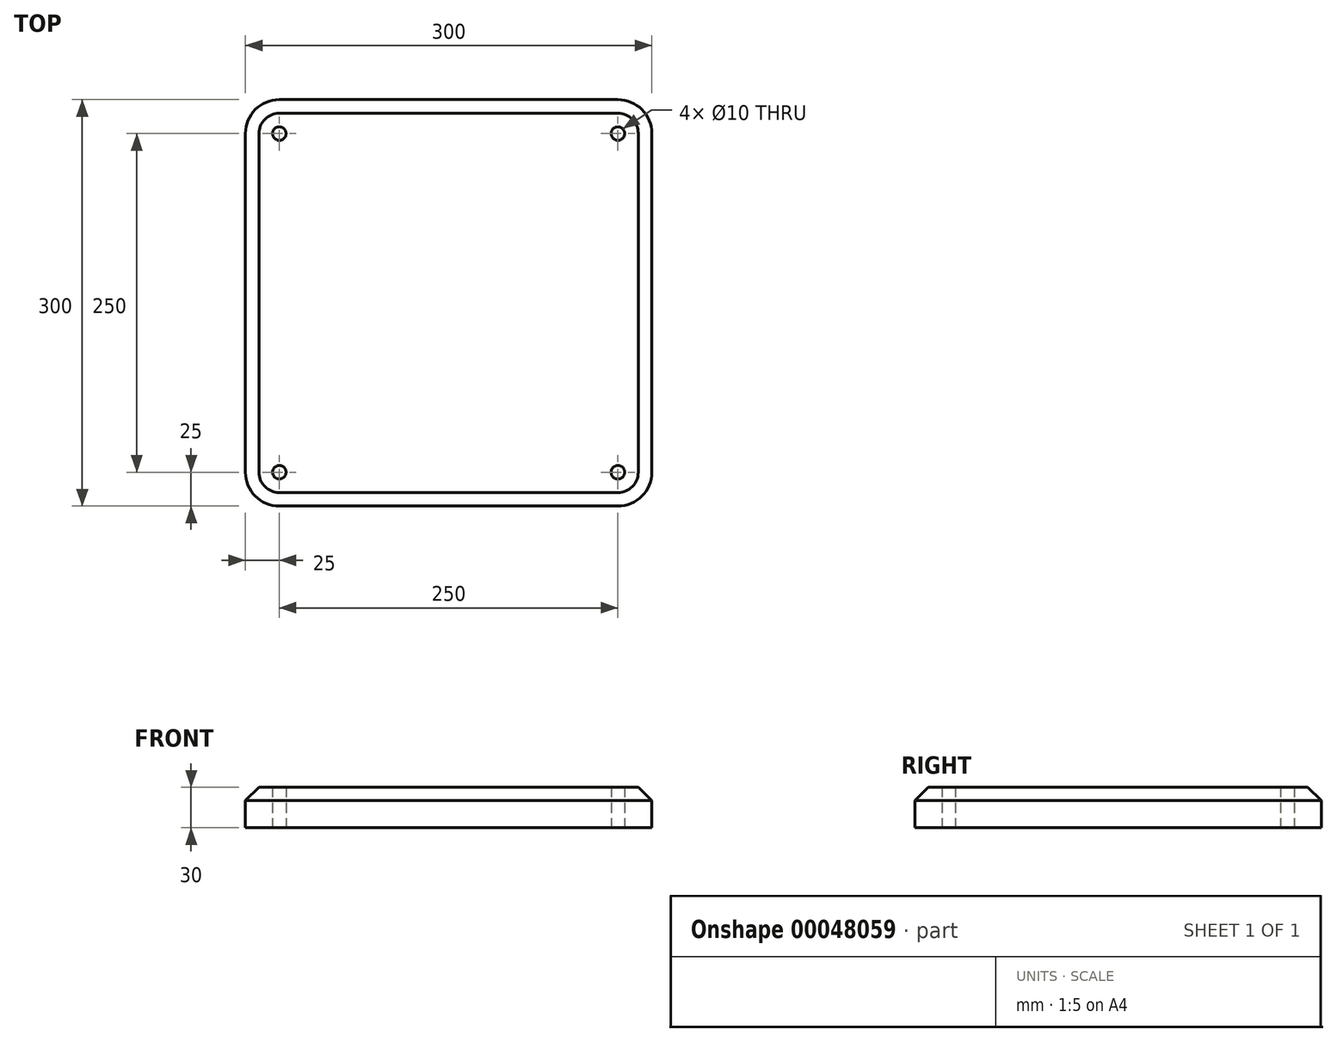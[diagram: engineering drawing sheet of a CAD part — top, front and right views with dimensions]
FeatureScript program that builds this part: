
annotation { "Feature Type Name" : "Feature", "Feature Type Description" : "" }
export const myFeature = defineFeature(function(context is Context, id is Id, definition is map)
    precondition{}
    {
        {
            var Q0;
            Q0=qCreatedBy(makeId("Top.planeOp"),FACE);
            var sketch = newSketch(context, id + "F0", { "sketchPlane" : qUnion([Q0])});
            skLineSegment(sketch, "E0.bottom", {"start": v(0, 0) * mm, "end": v(300, 0) * mm});
            skLineSegment(sketch, "E0.top", {"start": v(0, 300) * mm, "end": v(300, 300) * mm});
            skLineSegment(sketch, "E0.left", {"start": v(0, 0) * mm, "end": v(0, 300) * mm});
            skLineSegment(sketch, "E0.right", {"start": v(300, 0) * mm, "end": v(300, 300) * mm});
            skLineSegment(sketch, "E1.bottom", {"start": v(25, 275) * mm, "end": v(275, 275) * mm, "construction": true});
            skLineSegment(sketch, "E1.top", {"start": v(25, 25) * mm, "end": v(275, 25) * mm, "construction": true});
            skLineSegment(sketch, "E1.left", {"start": v(25, 275) * mm, "end": v(25, 25) * mm, "construction": true});
            skLineSegment(sketch, "E1.right", {"start": v(275, 275) * mm, "end": v(275, 25) * mm, "construction": true});
            skLineSegment(sketch, "E2", {"start": v(0, 0) * mm, "end": v(300, 300) * mm, "construction": true});
            skLineSegment(sketch, "E3", {"start": v(0, 300) * mm, "end": v(300, 0) * mm, "construction": true});
            skSolve(sketch);
        }
        {
            var Q0;
            Q0=makeQuery(id+"F0.imprint","IMPRINT",FACE,{"disambiguationData":[TD([[makeQuery(id+"F0.imprint","IMPRINT",EDGE,{"derivedFrom":sQuery(id+"F0.wireOp",EDGE,"E0.bottom")}),1.0]])]});
            extrude(context, id + "F1", {"entities" : qUnion([Q0]), "depth" : 30 * mm});
        }
        {
            var Q0;
            Q0=sQuery(id+"F0.wireOp",VERTEX,"E1.right.start");
            var Q1;
            Q1=sQuery(id+"F0.wireOp",VERTEX,"E1.left.start");
            var Q2;
            Q2=sQuery(id+"F0.wireOp",VERTEX,"E1.right.end");
            var Q3;
            Q3=sQuery(id+"F0.wireOp",VERTEX,"E1.left.end");
            var Q4;
            Q4=makeQuery(id+"F1.opExtrude","SWEPT_BODY",BODY,{"disambiguationData":[OSD([sQuery(id+"F0.wireOp",EDGE,"E0.bottom"),sQuery(id+"F0.wireOp",EDGE,"E0.top"),sQuery(id+"F0.wireOp",EDGE,"E0.left"),sQuery(id+"F0.wireOp",EDGE,"E0.right")])]});
            hole(context, id + "F2", {"style" : HoleStyle.SIMPLE, "holeDiameter" : 10 * mm, "endStyle" : HoleEndStyle.THROUGH, "oppositeDirection" : true, "locations" : qUnion([Q0, Q1, Q2, Q3]), "scope" : qUnion([Q4])});
        }
        {
            var Q0;
            Q0=makeQuery(id+"F1.opExtrude","SWEPT_EDGE",EDGE,{"disambiguationData":[OSD([sQuery(id+"F0.wireOp",EDGE,"E0.top"),sQuery(id+"F0.wireOp",EDGE,"E0.left")])]});
            var Q1;
            Q1=makeQuery(id+"F1.opExtrude","SWEPT_EDGE",EDGE,{"disambiguationData":[OSD([sQuery(id+"F0.wireOp",EDGE,"E0.bottom"),sQuery(id+"F0.wireOp",EDGE,"E0.left")])]});
            var Q2;
            Q2=makeQuery(id+"F1.opExtrude","SWEPT_EDGE",EDGE,{"disambiguationData":[OSD([sQuery(id+"F0.wireOp",EDGE,"E0.bottom"),sQuery(id+"F0.wireOp",EDGE,"E0.right")])]});
            var Q3;
            Q3=makeQuery(id+"F1.opExtrude","SWEPT_EDGE",EDGE,{"disambiguationData":[OSD([sQuery(id+"F0.wireOp",EDGE,"E0.top"),sQuery(id+"F0.wireOp",EDGE,"E0.right")])]});
            fillet(context, id + "F3", {"entities" : qUnion([Q0, Q1, Q2, Q3]), "radius" : 25 * mm, "tangentPropagation" : true, "allowEdgeOverflow" : false});
        }
        {
            var Q0;
            Q0=makeQuery(id+"F1.opExtrude","CAP_EDGE",EDGE,{"disambiguationData":[OSD([sQuery(id+"F0.wireOp",EDGE,"E0.left")])],"isStart":false});
            chamfer(context, id + "F4", {"entities" : qUnion([Q0]), "chamferType" : ChamferType.OFFSET_ANGLE, "width" : 10 * mm, "oppositeDirection" : false, "angle" : 45 * degree, "tangentPropagation" : true});
        }
    });
